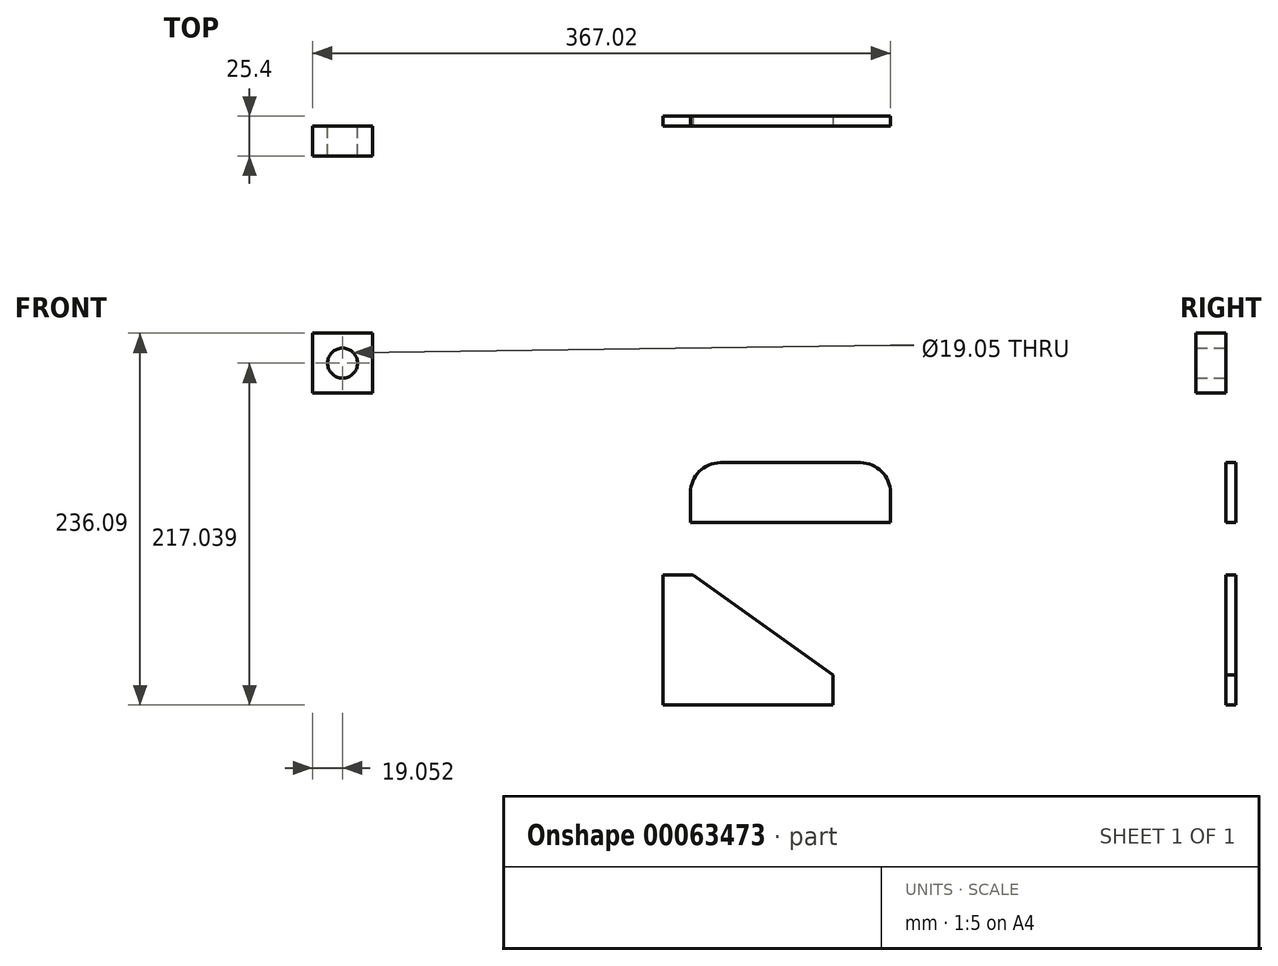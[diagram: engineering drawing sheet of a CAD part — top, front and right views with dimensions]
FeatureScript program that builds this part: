
annotation { "Feature Type Name" : "Feature", "Feature Type Description" : "" }
export const myFeature = defineFeature(function(context is Context, id is Id, definition is map)
    precondition{}
    {
        {
            var Q0;
            Q0=qCreatedBy(makeId("Front.planeOp"),FACE);
            var sketch = newSketch(context, id + "F0", { "sketchPlane" : qUnion([Q0])});
            skLineSegment(sketch, "E0", {"start": v(-47.1, 29.06) * mm, "end": v(-66.15, 29.06) * mm});
            skLineSegment(sketch, "E1", {"start": v(-66.15, 29.06) * mm, "end": v(-66.15, -53.49) * mm});
            skLineSegment(sketch, "E2", {"start": v(-66.15, -53.49) * mm, "end": v(41.8, -53.49) * mm});
            skLineSegment(sketch, "E3", {"start": v(41.8, -53.49) * mm, "end": v(41.8, -34.44) * mm});
            skLineSegment(sketch, "E4", {"start": v(-47.1, 29.06) * mm, "end": v(41.8, -34.44) * mm});
            skSolve(sketch);
        }
        {
            var Q0;
            Q0=makeQuery(id+"F0.imprint","IMPRINT",FACE,{"disambiguationData":[TD([[makeQuery(id+"F0.imprint","IMPRINT",EDGE,{"derivedFrom":sQuery(id+"F0.wireOp",EDGE,"E0")}),1.0]])]});
            extrude(context, id + "F1", {"entities" : qUnion([Q0]), "oppositeDirection" : true, "depth" : 6.35 * mm});
        }
        {
            var Q0;
            Q0=qCreatedBy(makeId("Front.planeOp"),FACE);
            var sketch = newSketch(context, id + "F2", { "sketchPlane" : qUnion([Q0])});
            skLineSegment(sketch, "E5", {"start": v(78.4, 62.24) * mm, "end": v(-48.6, 62.24) * mm});
            skLineSegment(sketch, "E6", {"start": v(-48.6, 62.24) * mm, "end": v(-48.6, 81.29) * mm});
            skLineSegment(sketch, "E7", {"start": v(-29.55, 100.34) * mm, "end": v(59.35, 100.34) * mm});
            skLineSegment(sketch, "E8", {"start": v(78.4, 81.29) * mm, "end": v(78.4, 62.24) * mm});
            skPoint(sketch, "E9.visualSharp", {"position": v(78.4, 100.34) * mm});
            skArc(sketch, "E9.filletArc", {"start": v(78.4, 81.29) * mm, "mid": v(72.82, 94.76) * mm, "end": v(59.35, 100.34) * mm});
            skPoint(sketch, "E10.visualSharp", {"position": v(-48.6, 100.34) * mm});
            skArc(sketch, "E10.filletArc", {"start": v(-29.55, 100.34) * mm, "mid": v(-43.02, 94.76) * mm, "end": v(-48.6, 81.29) * mm});
            skSolve(sketch);
        }
        {
            var Q0;
            Q0=makeQuery(id+"F2.imprint","IMPRINT",FACE,{"disambiguationData":[TD([[makeQuery(id+"F2.imprint","IMPRINT",EDGE,{"derivedFrom":sQuery(id+"F2.wireOp",EDGE,"E5")}),-1.0]])]});
            extrude(context, id + "F3", {"entities" : qUnion([Q0]), "oppositeDirection" : true, "depth" : 6.35 * mm});
        }
        {
            var Q0;
            Q0=qCreatedBy(makeId("Front.planeOp"),FACE);
            var sketch = newSketch(context, id + "F4", { "sketchPlane" : qUnion([Q0])});
            skLineSegment(sketch, "E11.bottom", {"start": v(-627.06, 185.58) * mm, "end": v(-341.31, 185.58) * mm});
            skLineSegment(sketch, "E11.top", {"start": v(-627.06, -73.38) * mm, "end": v(-341.31, -73.38) * mm});
            skLineSegment(sketch, "E11.left", {"start": v(-627.06, 185.58) * mm, "end": v(-627.06, -73.38) * mm});
            skLineSegment(sketch, "E11.right", {"start": v(-341.31, 185.58) * mm, "end": v(-341.31, -73.38) * mm});
            skSolve(sketch);
        }
        {
            var Q0;
            Q0=makeQuery(id+"F4.imprint","IMPRINT",FACE,{"disambiguationData":[TD([[makeQuery(id+"F4.imprint","IMPRINT",EDGE,{"derivedFrom":sQuery(id+"F4.wireOp",EDGE,"E11.bottom")}),-1.0]])]});
            extrude(context, id + "F5", {"entities" : qUnion([Q0]), "depth" : 19.05 * mm});
        }
        {
            var Q0;
            Q0=qCreatedBy(makeId("Front.planeOp"),FACE);
            var sketch = newSketch(context, id + "F6", { "sketchPlane" : qUnion([Q0])});
            skLineSegment(sketch, "E12.bottom", {"start": v(-250.52, 144.5) * mm, "end": v(-288.62, 144.5) * mm});
            skLineSegment(sketch, "E12.top", {"start": v(-250.52, 182.6) * mm, "end": v(-288.62, 182.6) * mm});
            skLineSegment(sketch, "E12.left", {"start": v(-250.52, 144.5) * mm, "end": v(-250.52, 182.6) * mm});
            skLineSegment(sketch, "E12.right", {"start": v(-288.62, 144.5) * mm, "end": v(-288.62, 182.6) * mm});
            skCircle(sketch, "E13", {"center": v(-269.57, 163.55) * mm, "radius": 9.53 * mm});
            skPoint(sketch, "E13.centerSnap0", {"position": v(-269.57, 182.6) * mm});
            skPoint(sketch, "E13.centerSnap1", {"position": v(-288.62, 163.55) * mm});
            skSolve(sketch);
        }
        {
            var Q0;
            Q0=makeQuery(id+"F6.imprint","IMPRINT",FACE,{"disambiguationData":[TD([[makeQuery(id+"F6.imprint","IMPRINT",EDGE,{"derivedFrom":sQuery(id+"F6.wireOp",EDGE,"E12.bottom")}),-1.0]])]});
            extrude(context, id + "F7", {"entities" : qUnion([Q0]), "depth" : 19.05 * mm});
        }
        {
            var Q0;
            Q0=makeQuery(id+"F5.opExtrude","SWEPT_BODY",BODY,{"disambiguationData":[OSD([sQuery(id+"F4.wireOp",EDGE,"E11.bottom"),sQuery(id+"F4.wireOp",EDGE,"E11.top"),sQuery(id+"F4.wireOp",EDGE,"E11.left"),sQuery(id+"F4.wireOp",EDGE,"E11.right")])]});
            deleteBodies(context, id + "F8", {"entities" : qUnion([Q0])});
        }
    });
